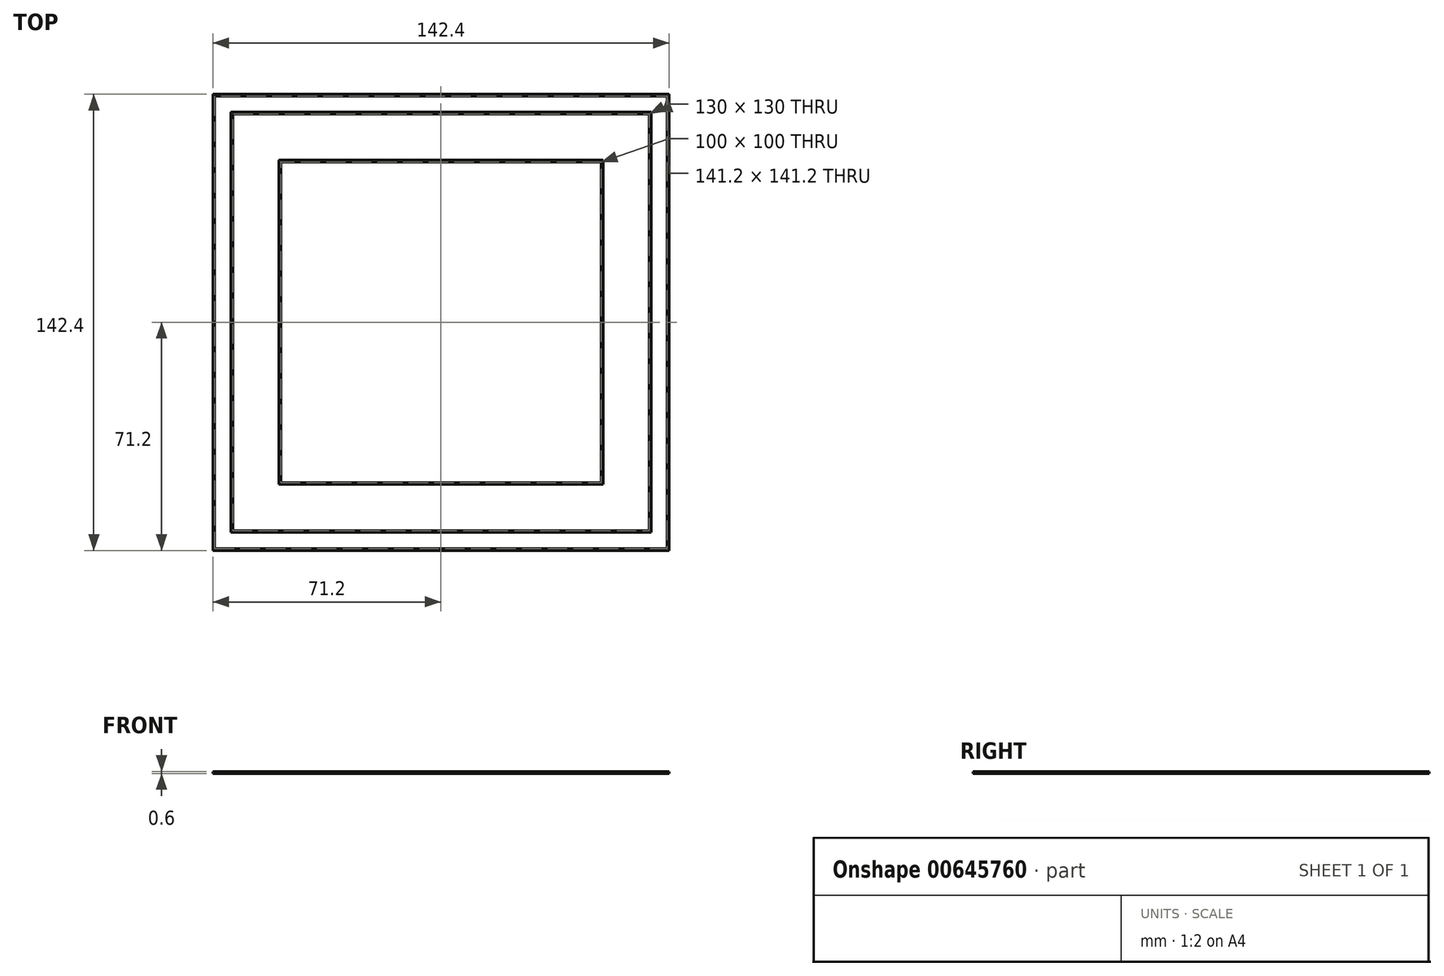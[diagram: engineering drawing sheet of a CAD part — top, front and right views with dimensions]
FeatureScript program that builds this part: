
annotation { "Feature Type Name" : "Feature", "Feature Type Description" : "" }
export const myFeature = defineFeature(function(context is Context, id is Id, definition is map)
    precondition{}
    {
        {
            var Q0;
            Q0=qCreatedBy(makeId("Top.planeOp"),FACE);
            var sketch = newSketch(context, id + "F0", { "sketchPlane" : qUnion([Q0])});
            skLineSegment(sketch, "E0.bottom", {"start": v(65, -65) * mm, "end": v(-65, -65) * mm});
            skLineSegment(sketch, "E0.top", {"start": v(65, 65) * mm, "end": v(-65, 65) * mm});
            skLineSegment(sketch, "E0.left", {"start": v(65, -65) * mm, "end": v(65, 65) * mm});
            skLineSegment(sketch, "E0.right", {"start": v(-65, -65) * mm, "end": v(-65, 65) * mm});
            skPoint(sketch, "E0.middle", {"position": v(0, 0) * mm});
            skLineSegment(sketch, "E1.0", {"start": v(65.6, 65.6) * mm, "end": v(-65.6, 65.6) * mm});
            skLineSegment(sketch, "E1.1", {"start": v(65.6, -65.6) * mm, "end": v(65.6, 65.6) * mm});
            skLineSegment(sketch, "E1.2", {"start": v(65.6, -65.6) * mm, "end": v(-65.6, -65.6) * mm});
            skLineSegment(sketch, "E1.3", {"start": v(-65.6, -65.6) * mm, "end": v(-65.6, 65.6) * mm});
            skLineSegment(sketch, "E2.bottom", {"start": v(50, -50) * mm, "end": v(-50, -50) * mm});
            skLineSegment(sketch, "E2.top", {"start": v(50, 50) * mm, "end": v(-50, 50) * mm});
            skLineSegment(sketch, "E2.left", {"start": v(50, -50) * mm, "end": v(50, 50) * mm});
            skLineSegment(sketch, "E2.right", {"start": v(-50, -50) * mm, "end": v(-50, 50) * mm});
            skLineSegment(sketch, "E3.0", {"start": v(50.6, 50.6) * mm, "end": v(-50.6, 50.6) * mm});
            skLineSegment(sketch, "E3.1", {"start": v(50.6, -50.6) * mm, "end": v(50.6, 50.6) * mm});
            skLineSegment(sketch, "E3.2", {"start": v(50.6, -50.6) * mm, "end": v(-50.6, -50.6) * mm});
            skLineSegment(sketch, "E3.3", {"start": v(-50.6, -50.6) * mm, "end": v(-50.6, 50.6) * mm});
            skLineSegment(sketch, "E4.0", {"start": v(-70.6, -70.6) * mm, "end": v(-70.6, 70.6) * mm});
            skLineSegment(sketch, "E4.1", {"start": v(70.6, -70.6) * mm, "end": v(-70.6, -70.6) * mm});
            skLineSegment(sketch, "E4.2", {"start": v(70.6, -70.6) * mm, "end": v(70.6, 70.6) * mm});
            skLineSegment(sketch, "E4.3", {"start": v(70.6, 70.6) * mm, "end": v(-70.6, 70.6) * mm});
            skLineSegment(sketch, "E5.0", {"start": v(71.2, 71.2) * mm, "end": v(-71.2, 71.2) * mm});
            skLineSegment(sketch, "E5.1", {"start": v(71.2, -71.2) * mm, "end": v(71.2, 71.2) * mm});
            skLineSegment(sketch, "E5.2", {"start": v(71.2, -71.2) * mm, "end": v(-71.2, -71.2) * mm});
            skLineSegment(sketch, "E5.3", {"start": v(-71.2, -71.2) * mm, "end": v(-71.2, 71.2) * mm});
            skSolve(sketch);
        }
        {
            var Q0;
            Q0 = qSketchRegion(id + "F0", true);
            var Q1;
            Q1=makeQuery(id+"F0.imprint","IMPRINT",FACE,{"disambiguationData":[TD([[makeQuery(id+"F0.imprint","IMPRINT",EDGE,{"derivedFrom":sQuery(id+"F0.wireOp",EDGE,"E4.0")}),1.0]])]});
            var Q2;
            Q2=makeQuery(id+"F0.imprint","IMPRINT",FACE,{"disambiguationData":[TD([[makeQuery(id+"F0.imprint","IMPRINT",EDGE,{"derivedFrom":sQuery(id+"F0.wireOp",EDGE,"E2.bottom")}),1.0]])]});
            var Q3;
            Q3=makeQuery(id+"F0.imprint","IMPRINT",FACE,{"disambiguationData":[TD([[makeQuery(id+"F0.imprint","IMPRINT",EDGE,{"derivedFrom":sQuery(id+"F0.wireOp",EDGE,"E0.bottom")}),1.0]])]});
            extrude(context, id + "F1", {"entities" : qUnion([Q0, Q1, Q2, Q3]), "depth" : 0.6 * mm, "offsetDistance" : 25 * mm});
        }
    });
